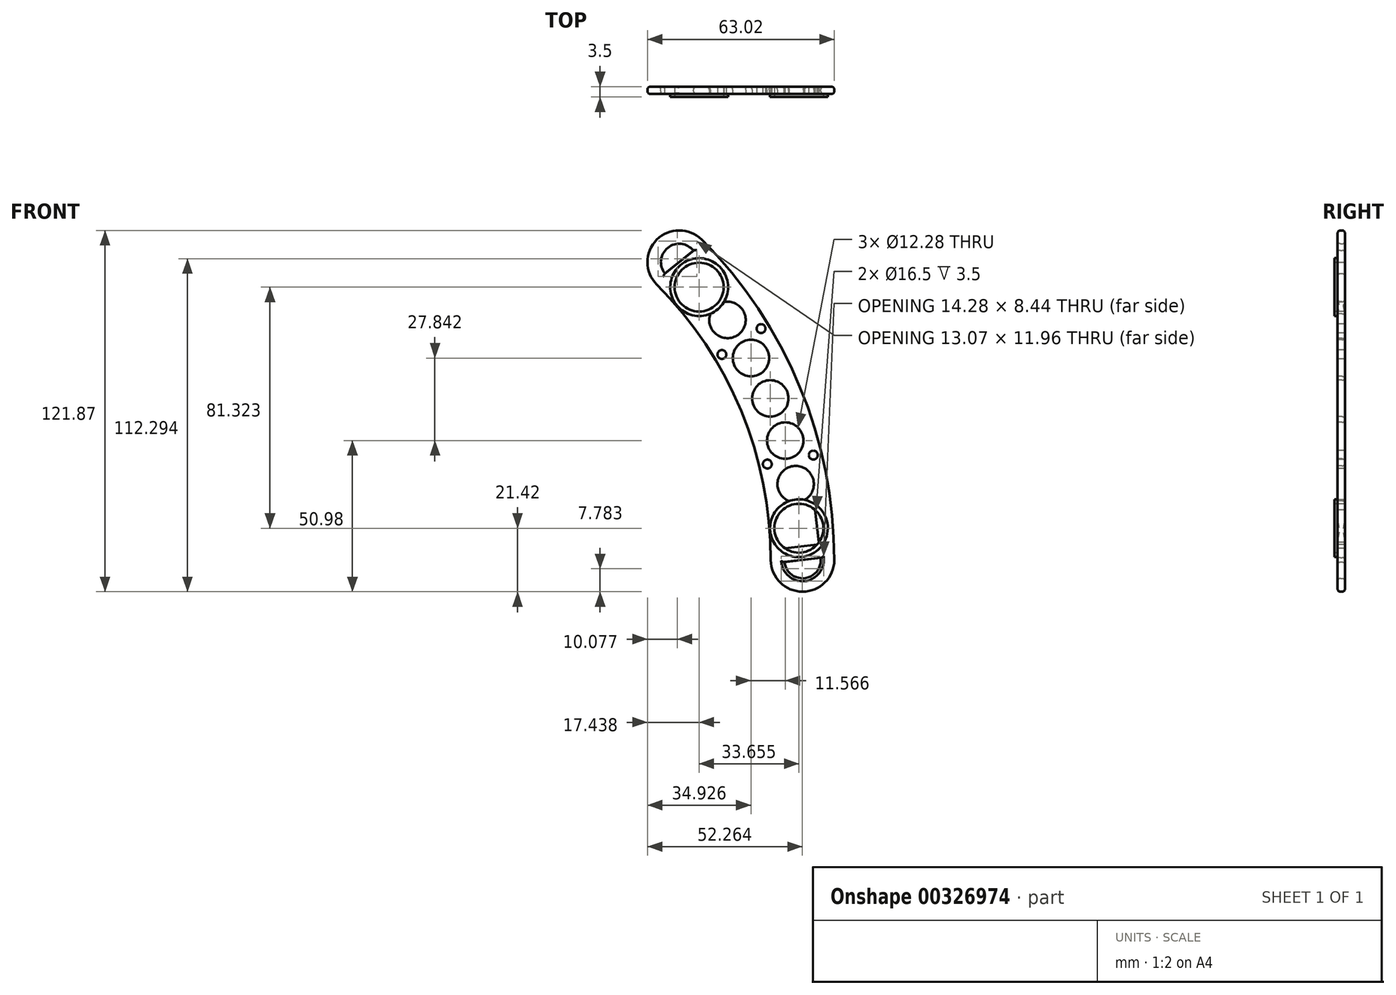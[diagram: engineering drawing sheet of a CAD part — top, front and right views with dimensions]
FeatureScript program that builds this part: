
annotation { "Feature Type Name" : "Feature", "Feature Type Description" : "" }
export const myFeature = defineFeature(function(context is Context, id is Id, definition is map)
    precondition{}
    {
        {
            var Q0;
            Q0=qCreatedBy(makeId("Front.planeOp"),FACE);
            var sketch = newSketch(context, id + "F0", { "sketchPlane" : qUnion([Q0])});
            skCircle(sketch, "E0", {"center": v(0, 0) * mm, "radius": 152.8 * mm});
            skCircle(sketch, "E1", {"center": v(0, 0) * mm, "radius": 131.4 * mm});
            skLineSegment(sketch, "E2", {"start": v(0, 0) * mm, "end": v(152.8, 0) * mm, "construction": true});
            skLineSegment(sketch, "E3", {"start": v(0, 0) * mm, "end": v(108.04, 108.04) * mm, "construction": true});
            skPoint(sketch, "E4", {"position": v(92.9, 92.9) * mm});
            skPoint(sketch, "E5", {"position": v(108.04, 108.04) * mm});
            skPoint(sketch, "E6", {"position": v(131.4, 0) * mm});
            skPoint(sketch, "E7", {"position": v(152.8, 0) * mm});
            skCircle(sketch, "E8", {"center": v(100.47, 100.47) * mm, "radius": 10.7 * mm});
            skCircle(sketch, "E9", {"center": v(142.1, 0) * mm, "radius": 10.7 * mm});
            skLineSegment(sketch, "E10", {"start": v(142.1, 0) * mm, "end": v(148.23, 0.7) * mm});
            skLineSegment(sketch, "E11", {"start": v(142.1, 0) * mm, "end": v(135.94, -0.7) * mm});
            skLineSegment(sketch, "E12", {"start": v(148.23, 0.7) * mm, "end": v(144.58, 32.71) * mm});
            skLineSegment(sketch, "E13", {"start": v(135.94, -0.7) * mm, "end": v(132.3, 31.31) * mm});
            skLineSegment(sketch, "E14", {"start": v(132.3, 31.31) * mm, "end": v(144.58, 32.71) * mm});
            skLineSegment(sketch, "E15", {"start": v(100.47, 100.47) * mm, "end": v(105.3, 104.33) * mm});
            skLineSegment(sketch, "E16", {"start": v(100.47, 100.47) * mm, "end": v(95.64, 96.62) * mm});
            skLineSegment(sketch, "E17", {"start": v(120.53, 75.25) * mm, "end": v(125.41, 79.16) * mm});
            skLineSegment(sketch, "E18", {"start": v(120.53, 75.25) * mm, "end": v(115.75, 71.44) * mm});
            skLineSegment(sketch, "E19", {"start": v(105.3, 104.33) * mm, "end": v(125.41, 79.16) * mm});
            skLineSegment(sketch, "E20", {"start": v(95.64, 96.62) * mm, "end": v(115.75, 71.44) * mm});
            skLineSegment(sketch, "E21", {"start": v(135.42, 3.88) * mm, "end": v(147.7, 5.28) * mm});
            skLineSegment(sketch, "E22", {"start": v(132.82, 26.73) * mm, "end": v(145.1, 28.13) * mm});
            skLineSegment(sketch, "E23", {"start": v(112.88, 75.04) * mm, "end": v(122.53, 82.76) * mm});
            skLineSegment(sketch, "E24", {"start": v(98.52, 93.01) * mm, "end": v(108.18, 100.73) * mm});
            skCircle(sketch, "E25", {"center": v(0, 0) * mm, "radius": 148.23 * mm, "construction": true});
            skCircle(sketch, "E26", {"center": v(0, 0) * mm, "radius": 135.95 * mm, "construction": true});
            skCircle(sketch, "E27", {"center": v(141.82, 2.29) * mm, "radius": 1 * mm});
            skCircle(sketch, "E28", {"center": v(138.7, 29.72) * mm, "radius": 1 * mm});
            skCircle(sketch, "E29", {"center": v(140.86, 10.72) * mm, "radius": 6.18 * mm});
            skLineSegment(sketch, "E30", {"start": v(122.53, 82.76) * mm, "end": v(115.75, 71.44) * mm, "construction": true});
            skLineSegment(sketch, "E31", {"start": v(112.88, 75.04) * mm, "end": v(125.41, 79.16) * mm, "construction": true});
            skCircle(sketch, "E32", {"center": v(101.91, 98.67) * mm, "radius": 1 * mm});
            skCircle(sketch, "E33", {"center": v(119.14, 77.1) * mm, "radius": 1 * mm});
            skCircle(sketch, "E34", {"center": v(107.2, 92.04) * mm, "radius": 6.18 * mm});
            skLineSegment(sketch, "E35", {"start": v(132.82, 26.73) * mm, "end": v(144.58, 32.71) * mm, "construction": true});
            skLineSegment(sketch, "E36", {"start": v(145.1, 28.13) * mm, "end": v(132.3, 31.31) * mm, "construction": true});
            skCircle(sketch, "E37", {"center": v(100.47, 100.47) * mm, "radius": 6.18 * mm});
            skCircle(sketch, "E38", {"center": v(142.1, 0) * mm, "radius": 6.19 * mm});
            skLineSegment(sketch, "E39", {"start": v(135.42, 3.88) * mm, "end": v(148.23, 0.7) * mm, "construction": true});
            skLineSegment(sketch, "E40", {"start": v(147.7, 5.28) * mm, "end": v(135.94, -0.7) * mm, "construction": true});
            skLineSegment(sketch, "E41", {"start": v(148.23, 0.7) * mm, "end": v(148.24, 0.7) * mm});
            skSolve(sketch);
        }
        {
            var Q0;
            {var subQ16=sQuery(id+"F0.wireOp",EDGE,"E18");Q0=makeQuery(id+"F0.imprint","IMPRINT",FACE,{"disambiguationData":[TD([[makeQuery(id+"F0.imprint","IMPRINT",EDGE,{"derivedFrom":subQ16}),1.0]])]});}
            var Q1;
            {var subQ14=sQuery(id+"F0.wireOp",EDGE,"E17");Q1=makeQuery(id+"F0.imprint","IMPRINT",FACE,{"disambiguationData":[TD([[makeQuery(id+"F0.imprint","IMPRINT",EDGE,{"derivedFrom":subQ14}),-1.0]])]});}
            var Q2;
            {var subQ3=sQuery(id+"F0.wireOp",EDGE,"oQQra7B9-EMDj-B2YQ-GpEd-beqhVWcHA2Qh");var subQ5=sQuery(id+"F0.wireOp",EDGE,"E22");var subQ9=makeQuery(id+"F0.imprint","INTERSECT",VERTEX,{"derivedFrom":[subQ3,subQ5]});Q2=makeQuery(id+"F0.imprint","IMPRINT",FACE,{"disambiguationData":[TD([[makeQuery(id+"F0.imprint","IMPRINT",EDGE,{"disambiguationData":[TD([[subQ9,-1.0]])],"derivedFrom":subQ3}),-1.0]])]});}
            var Q3;
            {var subQ3=sQuery(id+"F0.wireOp",EDGE,"oQQra7B9-EMDj-B2YQ-GpEd-beqhVWcHA2Qh");var subQ5=sQuery(id+"F0.wireOp",EDGE,"E22");var subQ9=makeQuery(id+"F0.imprint","INTERSECT",VERTEX,{"derivedFrom":[subQ3,subQ5]});Q3=makeQuery(id+"F0.imprint","IMPRINT",FACE,{"disambiguationData":[TD([[makeQuery(id+"F0.imprint","IMPRINT",EDGE,{"disambiguationData":[TD([[subQ9,-1.0]])],"derivedFrom":subQ3}),1.0]])]});}
            var Q4;
            {var subQ5=sQuery(id+"F0.wireOp",EDGE,"E9");var subQ8=makeQuery(id+"F0.imprint","INTERSECT",VERTEX,{"derivedFrom":[sQuery(id+"F0.wireOp",EDGE,"E1"),subQ5]});Q4=makeQuery(id+"F0.imprint","IMPRINT",FACE,{"disambiguationData":[TD([[makeQuery(id+"F0.imprint","IMPRINT",EDGE,{"disambiguationData":[TD([[subQ8,1.0]])],"derivedFrom":subQ5}),1.0]])]});}
            var Q5;
            {var subQ1=sQuery(id+"F0.wireOp",EDGE,"E9");var subQ5=makeQuery(id+"F0.imprint","INTERSECT",VERTEX,{"derivedFrom":[sQuery(id+"F0.wireOp",EDGE,"E0"),subQ1]});Q5=makeQuery(id+"F0.imprint","IMPRINT",FACE,{"disambiguationData":[TD([[makeQuery(id+"F0.imprint","IMPRINT",EDGE,{"disambiguationData":[TD([[subQ5,-1.0]])],"derivedFrom":subQ1}),1.0]])]});}
            var Q6;
            {var subQ1=sQuery(id+"F0.wireOp",EDGE,"E13");var subQ3=sQuery(id+"F0.wireOp",EDGE,"E21");var subQ4=makeQuery(id+"F0.imprint","INTERSECT",VERTEX,{"derivedFrom":[subQ1,subQ3]});Q6=makeQuery(id+"F0.imprint","IMPRINT",FACE,{"disambiguationData":[TD([[makeQuery(id+"F0.imprint","IMPRINT",EDGE,{"disambiguationData":[TD([[subQ4,-1.0]])],"derivedFrom":subQ3}),-1.0]])]});}
            var Q7;
            {var subQ1=sQuery(id+"F0.wireOp",EDGE,"E12");var subQ3=sQuery(id+"F0.wireOp",EDGE,"E21");var subQ4=makeQuery(id+"F0.imprint","INTERSECT",VERTEX,{"derivedFrom":[subQ1,subQ3]});Q7=makeQuery(id+"F0.imprint","IMPRINT",FACE,{"disambiguationData":[TD([[makeQuery(id+"F0.imprint","IMPRINT",EDGE,{"disambiguationData":[TD([[subQ4,1.0]])],"derivedFrom":subQ3}),-1.0]])]});}
            var Q8;
            {var subQ4=sQuery(id+"F0.wireOp",EDGE,"E8");var subQ5=makeQuery(id+"F0.imprint","INTERSECT",VERTEX,{"derivedFrom":[sQuery(id+"F0.wireOp",EDGE,"E0"),subQ4]});Q8=makeQuery(id+"F0.imprint","IMPRINT",FACE,{"disambiguationData":[TD([[makeQuery(id+"F0.imprint","IMPRINT",EDGE,{"disambiguationData":[TD([[subQ5,-1.0]])],"derivedFrom":subQ4}),1.0]])]});}
            var Q9;
            {var subQ5=sQuery(id+"F0.wireOp",EDGE,"E8");var subQ9=makeQuery(id+"F0.imprint","INTERSECT",VERTEX,{"derivedFrom":[sQuery(id+"F0.wireOp",EDGE,"E1"),subQ5]});Q9=makeQuery(id+"F0.imprint","IMPRINT",FACE,{"disambiguationData":[TD([[makeQuery(id+"F0.imprint","IMPRINT",EDGE,{"disambiguationData":[TD([[subQ9,1.0]])],"derivedFrom":subQ5}),1.0]])]});}
            var Q10;
            {var subQ1=sQuery(id+"F0.wireOp",EDGE,"E20");var subQ3=sQuery(id+"F0.wireOp",EDGE,"E24");var subQ4=makeQuery(id+"F0.imprint","INTERSECT",VERTEX,{"derivedFrom":[subQ1,subQ3]});Q10=makeQuery(id+"F0.imprint","IMPRINT",FACE,{"disambiguationData":[TD([[makeQuery(id+"F0.imprint","IMPRINT",EDGE,{"disambiguationData":[TD([[subQ4,-1.0]])],"derivedFrom":subQ3}),1.0]])]});}
            var Q11;
            {var subQ4=sQuery(id+"F0.wireOp",EDGE,"E16");Q11=makeQuery(id+"F0.imprint","IMPRINT",FACE,{"disambiguationData":[TD([[makeQuery(id+"F0.imprint","IMPRINT",EDGE,{"derivedFrom":subQ4}),1.0]])]});}
            var Q12;
            {var subQ0=sQuery(id+"F0.wireOp",EDGE,"E15");Q12=makeQuery(id+"F0.imprint","IMPRINT",FACE,{"disambiguationData":[TD([[makeQuery(id+"F0.imprint","IMPRINT",EDGE,{"derivedFrom":subQ0}),-1.0]])]});}
            var Q13;
            {var subQ1=sQuery(id+"F0.wireOp",EDGE,"E19");var subQ3=sQuery(id+"F0.wireOp",EDGE,"E24");var subQ4=makeQuery(id+"F0.imprint","INTERSECT",VERTEX,{"derivedFrom":[subQ1,subQ3]});Q13=makeQuery(id+"F0.imprint","IMPRINT",FACE,{"disambiguationData":[TD([[makeQuery(id+"F0.imprint","IMPRINT",EDGE,{"disambiguationData":[TD([[subQ4,1.0]])],"derivedFrom":subQ3}),1.0]])]});}
            var Q14;
            {var subQ1=sQuery(id+"F0.wireOp",EDGE,"E18");Q14=makeQuery(id+"F0.imprint","IMPRINT",FACE,{"disambiguationData":[TD([[makeQuery(id+"F0.imprint","IMPRINT",EDGE,{"derivedFrom":subQ1}),-1.0]])]});}
            var Q15;
            {var subQ1=sQuery(id+"F0.wireOp",EDGE,"E17");Q15=makeQuery(id+"F0.imprint","IMPRINT",FACE,{"disambiguationData":[TD([[makeQuery(id+"F0.imprint","IMPRINT",EDGE,{"derivedFrom":subQ1}),1.0]])]});}
            var Q16;
            {var subQ0=sQuery(id+"F0.wireOp",EDGE,"E14");Q16=makeQuery(id+"F0.imprint","IMPRINT",FACE,{"disambiguationData":[TD([[makeQuery(id+"F0.imprint","IMPRINT",EDGE,{"derivedFrom":subQ0}),-1.0]])]});}
            var Q17;
            {var subQ5=sQuery(id+"F0.wireOp",EDGE,"E10");Q17=makeQuery(id+"F0.imprint","IMPRINT",FACE,{"disambiguationData":[TD([[makeQuery(id+"F0.imprint","IMPRINT",EDGE,{"derivedFrom":subQ5}),1.0]])]});}
            var Q18;
            Q18=makeQuery(id+"F0.imprint","IMPRINT",FACE,{"disambiguationData":[TD([[makeQuery(id+"F0.imprint","IMPRINT",EDGE,{"derivedFrom":sQuery(id+"F0.wireOp",EDGE,"E27")}),-1.0]])]});
            var Q19;
            {var subQ0=sQuery(id+"F0.wireOp",EDGE,"E41");Q19=makeQuery(id+"F0.imprint","IMPRINT",FACE,{"disambiguationData":[TD([[makeQuery(id+"F0.imprint","IMPRINT",EDGE,{"derivedFrom":subQ0}),1.0]])]});}
            extrude(context, id + "F1", {"entities" : qUnion([Q0, Q1, Q2, Q3, Q4, Q5, Q6, Q7, Q8, Q9, Q10, Q11, Q12, Q13, Q14, Q15, Q16, Q17, Q18, Q19]), "depth" : 2.5 * mm});
        }
        {
            var Q0;
            Q0=makeQuery(id+"F1.opExtrude","CAP_FACE",FACE,{"disambiguationData":[OSD([sQuery(id+"F0.wireOp",EDGE,"E0"),sQuery(id+"F0.wireOp",EDGE,"E1"),sQuery(id+"F0.wireOp",EDGE,"E8"),sQuery(id+"F0.wireOp",EDGE,"E9"),sQuery(id+"F0.wireOp",EDGE,"E10"),sQuery(id+"F0.wireOp",EDGE,"E11"),sQuery(id+"F0.wireOp",EDGE,"E12"),sQuery(id+"F0.wireOp",EDGE,"E13"),sQuery(id+"F0.wireOp",EDGE,"E15"),sQuery(id+"F0.wireOp",EDGE,"E16"),sQuery(id+"F0.wireOp",EDGE,"E19"),sQuery(id+"F0.wireOp",EDGE,"E20"),sQuery(id+"F0.wireOp",EDGE,"E21"),sQuery(id+"F0.wireOp",EDGE,"E22"),sQuery(id+"F0.wireOp",EDGE,"E23"),sQuery(id+"F0.wireOp",EDGE,"E24"),sQuery(id+"F0.wireOp",EDGE,"E27"),sQuery(id+"F0.wireOp",EDGE,"E28"),sQuery(id+"F0.wireOp",EDGE,"E32"),sQuery(id+"F0.wireOp",EDGE,"E33"),sQuery(id+"F0.wireOp",EDGE,"E37"),sQuery(id+"F0.wireOp",EDGE,"E38")])],"isStart":false});
            var sketch = newSketch(context, id + "F2", { "sketchPlane" : qUnion([Q0])});
            skCircle(sketch, "E42", {"center": v(136.26, 40.28) * mm, "radius": 6.14 * mm});
            skCircle(sketch, "E43", {"center": v(124.7, 68.12) * mm, "radius": 6.14 * mm});
            skCircle(sketch, "E44", {"center": v(131.22, 54.5) * mm, "radius": 6.14 * mm});
            skCircle(sketch, "E45", {"center": v(0, 0) * mm, "radius": 142.1 * mm, "construction": true});
            skLineSegment(sketch, "E46", {"start": v(0, 0) * mm, "end": v(136.26, 40.28) * mm, "construction": true});
            skLineSegment(sketch, "E47", {"start": v(0, 0) * mm, "end": v(131.22, 54.5) * mm, "construction": true});
            skLineSegment(sketch, "E48", {"start": v(0, 0) * mm, "end": v(124.7, 68.12) * mm, "construction": true});
            skCircle(sketch, "E49", {"center": v(0, 0) * mm, "radius": 152.8 * mm, "construction": true});
            skCircle(sketch, "E50", {"center": v(0, 0) * mm, "radius": 131.4 * mm, "construction": true});
            skCircle(sketch, "E51", {"center": v(0, 0) * mm, "radius": 135.95 * mm, "construction": true});
            skCircle(sketch, "E52", {"center": v(0, 0) * mm, "radius": 148.23 * mm, "construction": true});
            skLineSegment(sketch, "E53", {"start": v(112.88, 75.04) * mm, "end": v(119.3, 65.18) * mm, "construction": true});
            skLineSegment(sketch, "E54", {"start": v(119.3, 65.18) * mm, "end": v(118, 79.14) * mm, "construction": true});
            skLineSegment(sketch, "E55", {"start": v(118, 79.14) * mm, "end": v(130.08, 71.07) * mm, "construction": true});
            skLineSegment(sketch, "E56", {"start": v(130.08, 71.07) * mm, "end": v(122.53, 82.76) * mm, "construction": true});
            skLineSegment(sketch, "E57", {"start": v(122.53, 82.76) * mm, "end": v(118, 79.14) * mm});
            skLineSegment(sketch, "E58", {"start": v(112.88, 75.04) * mm, "end": v(118, 79.14) * mm});
            skLineSegment(sketch, "E59", {"start": v(126.3, 76.91) * mm, "end": v(130.43, 79.57) * mm, "construction": true});
            skCircle(sketch, "E60", {"center": v(128.1, 78.07) * mm, "radius": 1 * mm});
            skLineSegment(sketch, "E61", {"start": v(130.37, 38.54) * mm, "end": v(132.82, 26.73) * mm});
            skLineSegment(sketch, "E62", {"start": v(145.1, 28.13) * mm, "end": v(142.22, 41.78) * mm});
            skLineSegment(sketch, "E63", {"start": v(131.6, 32.64) * mm, "end": v(127.49, 31.79) * mm});
            skLineSegment(sketch, "E64", {"start": v(143.66, 34.96) * mm, "end": v(148.5, 35.98) * mm});
            skCircle(sketch, "E65", {"center": v(130.21, 32.35) * mm, "radius": 1 * mm});
            skCircle(sketch, "E66", {"center": v(145.71, 35.4) * mm, "radius": 1 * mm});
            skLineSegment(sketch, "E67", {"start": v(116.1, 70.11) * mm, "end": v(112.55, 67.8) * mm, "construction": true});
            skCircle(sketch, "E68", {"center": v(114.87, 69.32) * mm, "radius": 1 * mm});
            skLineSegment(sketch, "E69", {"start": v(0, 0) * mm, "end": v(116.76, 80.97) * mm, "construction": true});
            skLineSegment(sketch, "E70", {"start": v(0, 0) * mm, "end": v(139.77, 25.6) * mm, "construction": true});
            skCircle(sketch, "E71", {"center": v(139.77, 25.6) * mm, "radius": 6.14 * mm});
            skCircle(sketch, "E72", {"center": v(116.76, 80.97) * mm, "radius": 6.14 * mm});
            skSolve(sketch);
        }
        {
            var Q0;
            Q0=makeQuery(id+"F2.imprint","IMPRINT",FACE,{"disambiguationData":[TD([[makeQuery(id+"F2.imprint","IMPRINT",EDGE,{"derivedFrom":sQuery(id+"F2.wireOp",EDGE,"E43")}),1.0]])]});
            var Q1;
            Q1=makeQuery(id+"F2.imprint","IMPRINT",FACE,{"disambiguationData":[TD([[makeQuery(id+"F2.imprint","IMPRINT",EDGE,{"derivedFrom":sQuery(id+"F2.wireOp",EDGE,"E44")}),1.0]])]});
            var Q2;
            Q2=makeQuery(id+"F2.imprint","IMPRINT",FACE,{"disambiguationData":[TD([[makeQuery(id+"F2.imprint","IMPRINT",EDGE,{"derivedFrom":sQuery(id+"F2.wireOp",EDGE,"E42")}),1.0]])]});
            var Q3;
            {var subQ0=sQuery(id+"F2.wireOp",EDGE,"E56");var subQ1=sQuery(id+"F2.wireOp",EDGE,"E43");var subQ2=makeQuery(id+"F2.imprint","INTERSECT",VERTEX,{"derivedFrom":[subQ1,subQ0]});Q3=makeQuery(id+"F2.imprint","IMPRINT",FACE,{"disambiguationData":[TD([[makeQuery(id+"F2.imprint","IMPRINT",EDGE,{"disambiguationData":[TD([[subQ2,-1.0]])],"derivedFrom":subQ1}),1.0]])]});}
            var Q4;
            {var subQ0=sQuery(id+"F2.wireOp",EDGE,"E54");var subQ1=sQuery(id+"F2.wireOp",EDGE,"E43");var subQ3=makeQuery(id+"F2.imprint","INTERSECT",VERTEX,{"derivedFrom":[subQ1,subQ0]});Q4=makeQuery(id+"F2.imprint","IMPRINT",FACE,{"disambiguationData":[TD([[makeQuery(id+"F2.imprint","IMPRINT",EDGE,{"disambiguationData":[TD([[subQ3,-1.0]])],"derivedFrom":subQ1}),1.0]])]});}
            var Q5;
            Q5=makeQuery(id+"F2.imprint","IMPRINT",FACE,{"disambiguationData":[TD([[makeQuery(id+"F2.imprint","IMPRINT",EDGE,{"derivedFrom":sQuery(id+"F2.wireOp",EDGE,"6Q9i7ZKX-M5Zn-dDvE-S5ua-DKoOSJd4rO0q")}),1.0]])]});
            var Q6;
            Q6=makeQuery(id+"F2.imprint","IMPRINT",FACE,{"disambiguationData":[TD([[makeQuery(id+"F2.imprint","IMPRINT",EDGE,{"derivedFrom":sQuery(id+"F2.wireOp",EDGE,"E60")}),1.0]])]});
            var Q7;
            Q7=makeQuery(id+"F2.imprint","IMPRINT",FACE,{"disambiguationData":[TD([[makeQuery(id+"F2.imprint","IMPRINT",EDGE,{"derivedFrom":sQuery(id+"F2.wireOp",EDGE,"E68")}),1.0]])]});
            var Q8;
            {var subQ0=sQuery(id+"F2.wireOp",EDGE,"E66");var subQ1=sQuery(id+"F2.wireOp",EDGE,"E64");var subQ2=makeQuery(id+"F2.imprint","INTERSECT",VERTEX,{"disambiguationData":[OD(0.0)],"derivedFrom":[subQ1,subQ0]});Q8=makeQuery(id+"F2.imprint","IMPRINT",FACE,{"disambiguationData":[TD([[makeQuery(id+"F2.imprint","IMPRINT",EDGE,{"disambiguationData":[TD([[subQ2,-1.0]])],"derivedFrom":subQ1}),1.0]])]});}
            var Q9;
            {var subQ0=sQuery(id+"F2.wireOp",EDGE,"E66");var subQ1=sQuery(id+"F2.wireOp",EDGE,"E64");var subQ2=makeQuery(id+"F2.imprint","INTERSECT",VERTEX,{"disambiguationData":[OD(0.0)],"derivedFrom":[subQ1,subQ0]});Q9=makeQuery(id+"F2.imprint","IMPRINT",FACE,{"disambiguationData":[TD([[makeQuery(id+"F2.imprint","IMPRINT",EDGE,{"disambiguationData":[TD([[subQ2,-1.0]])],"derivedFrom":subQ1}),-1.0]])]});}
            var Q10;
            {var subQ0=sQuery(id+"F2.wireOp",EDGE,"E65");var subQ1=sQuery(id+"F2.wireOp",EDGE,"E63");var subQ2=makeQuery(id+"F2.imprint","INTERSECT",VERTEX,{"disambiguationData":[OD(0.0)],"derivedFrom":[subQ1,subQ0]});Q10=makeQuery(id+"F2.imprint","IMPRINT",FACE,{"disambiguationData":[TD([[makeQuery(id+"F2.imprint","IMPRINT",EDGE,{"disambiguationData":[TD([[subQ2,-1.0]])],"derivedFrom":subQ1}),1.0]])]});}
            var Q11;
            {var subQ0=sQuery(id+"F2.wireOp",EDGE,"E65");var subQ1=sQuery(id+"F2.wireOp",EDGE,"E63");var subQ2=makeQuery(id+"F2.imprint","INTERSECT",VERTEX,{"disambiguationData":[OD(0.0)],"derivedFrom":[subQ1,subQ0]});Q11=makeQuery(id+"F2.imprint","IMPRINT",FACE,{"disambiguationData":[TD([[makeQuery(id+"F2.imprint","IMPRINT",EDGE,{"disambiguationData":[TD([[subQ2,-1.0]])],"derivedFrom":subQ1}),-1.0]])]});}
            extrude(context, id + "F3", {"entities" : qUnion([Q0, Q1, Q2, Q3, Q4, Q5, Q6, Q7, Q8, Q9, Q10, Q11]), "operationType" : NewBodyOperationType.REMOVE, "oppositeDirection" : true, "depth" : 25 * mm});
        }
        {
            var Q0;
            Q0=makeQuery(id+"F1.opExtrude","CAP_EDGE",EDGE,{"disambiguationData":[OSD([sQuery(id+"F0.wireOp",EDGE,"E38")])],"isStart":true});
            var Q1;
            Q1=makeQuery(id+"F1.opExtrude","CAP_EDGE",EDGE,{"disambiguationData":[OSD([sQuery(id+"F0.wireOp",EDGE,"E38")])],"isStart":false});
            var Q2;
            Q2=makeQuery(id+"F1.opExtrude","CAP_EDGE",EDGE,{"disambiguationData":[OSD([sQuery(id+"F0.wireOp",EDGE,"E9")])],"isStart":true});
            var Q3;
            Q3=makeQuery(id+"F1.opExtrude","CAP_EDGE",EDGE,{"disambiguationData":[OSD([sQuery(id+"F0.wireOp",EDGE,"E0")])],"isStart":false});
            var Q4;
            Q4=makeQuery(id+"F1.opExtrude","CAP_EDGE",EDGE,{"disambiguationData":[OSD([sQuery(id+"F0.wireOp",EDGE,"E37")])],"isStart":false});
            var Q5;
            Q5=makeQuery(id+"F1.opExtrude","CAP_EDGE",EDGE,{"disambiguationData":[OSD([sQuery(id+"F0.wireOp",EDGE,"E37")])],"isStart":true});
            var Q6;
            Q6=makeQuery(id+"F3.boolean.opBoolean","COPY",EDGE,{"derivedFrom":makeQuery(id+"F3.opExtrude","CAP_EDGE",EDGE,{"disambiguationData":[OSD([sQuery(id+"F2.wireOp",EDGE,"E43")])],"isStart":true})});
            var Q7;
            Q7=makeQuery(id+"F3.boolean.opBoolean","COPY",EDGE,{"derivedFrom":makeQuery(id+"F3.opExtrude","CAP_EDGE",EDGE,{"disambiguationData":[OSD([sQuery(id+"F2.wireOp",EDGE,"E44")])],"isStart":true})});
            var Q8;
            Q8=makeQuery(id+"F3.boolean.opBoolean","COPY",EDGE,{"derivedFrom":makeQuery(id+"F3.opExtrude","CAP_EDGE",EDGE,{"disambiguationData":[OSD([sQuery(id+"F2.wireOp",EDGE,"E42")])],"isStart":true})});
            var Q9;
            Q9=makeQuery(id+"F3.boolean.opBoolean","INTERSECT",EDGE,{"derivedFrom":[makeQuery(id+"F1.opExtrude","CAP_FACE",FACE,{"disambiguationData":[OSD([sQuery(id+"F0.wireOp",EDGE,"E0"),sQuery(id+"F0.wireOp",EDGE,"E1"),sQuery(id+"F0.wireOp",EDGE,"E8"),sQuery(id+"F0.wireOp",EDGE,"E9"),sQuery(id+"F0.wireOp",EDGE,"E10"),sQuery(id+"F0.wireOp",EDGE,"E11"),sQuery(id+"F0.wireOp",EDGE,"E12"),sQuery(id+"F0.wireOp",EDGE,"E13"),sQuery(id+"F0.wireOp",EDGE,"E15"),sQuery(id+"F0.wireOp",EDGE,"E16"),sQuery(id+"F0.wireOp",EDGE,"E19"),sQuery(id+"F0.wireOp",EDGE,"E20"),sQuery(id+"F0.wireOp",EDGE,"E21"),sQuery(id+"F0.wireOp",EDGE,"E22"),sQuery(id+"F0.wireOp",EDGE,"E23"),sQuery(id+"F0.wireOp",EDGE,"E24"),sQuery(id+"F0.wireOp",EDGE,"E27"),sQuery(id+"F0.wireOp",EDGE,"E28"),sQuery(id+"F0.wireOp",EDGE,"E32"),sQuery(id+"F0.wireOp",EDGE,"E33"),sQuery(id+"F0.wireOp",EDGE,"E37"),sQuery(id+"F0.wireOp",EDGE,"E38")])],"isStart":true}),makeQuery(id+"F3.opExtrude","SWEPT_FACE",FACE,{"disambiguationData":[OSD([sQuery(id+"F2.wireOp",EDGE,"E43")])]})]});
            var Q10;
            Q10=makeQuery(id+"F3.boolean.opBoolean","INTERSECT",EDGE,{"derivedFrom":[makeQuery(id+"F1.opExtrude","CAP_FACE",FACE,{"disambiguationData":[OSD([sQuery(id+"F0.wireOp",EDGE,"E0"),sQuery(id+"F0.wireOp",EDGE,"E1"),sQuery(id+"F0.wireOp",EDGE,"E8"),sQuery(id+"F0.wireOp",EDGE,"E9"),sQuery(id+"F0.wireOp",EDGE,"E10"),sQuery(id+"F0.wireOp",EDGE,"E11"),sQuery(id+"F0.wireOp",EDGE,"E12"),sQuery(id+"F0.wireOp",EDGE,"E13"),sQuery(id+"F0.wireOp",EDGE,"E15"),sQuery(id+"F0.wireOp",EDGE,"E16"),sQuery(id+"F0.wireOp",EDGE,"E19"),sQuery(id+"F0.wireOp",EDGE,"E20"),sQuery(id+"F0.wireOp",EDGE,"E21"),sQuery(id+"F0.wireOp",EDGE,"E22"),sQuery(id+"F0.wireOp",EDGE,"E23"),sQuery(id+"F0.wireOp",EDGE,"E24"),sQuery(id+"F0.wireOp",EDGE,"E27"),sQuery(id+"F0.wireOp",EDGE,"E28"),sQuery(id+"F0.wireOp",EDGE,"E32"),sQuery(id+"F0.wireOp",EDGE,"E33"),sQuery(id+"F0.wireOp",EDGE,"E37"),sQuery(id+"F0.wireOp",EDGE,"E38")])],"isStart":true}),makeQuery(id+"F3.opExtrude","SWEPT_FACE",FACE,{"disambiguationData":[OSD([sQuery(id+"F2.wireOp",EDGE,"E44")])]})]});
            var Q11;
            Q11=makeQuery(id+"F3.boolean.opBoolean","INTERSECT",EDGE,{"derivedFrom":[makeQuery(id+"F1.opExtrude","CAP_FACE",FACE,{"disambiguationData":[OSD([sQuery(id+"F0.wireOp",EDGE,"E0"),sQuery(id+"F0.wireOp",EDGE,"E1"),sQuery(id+"F0.wireOp",EDGE,"E8"),sQuery(id+"F0.wireOp",EDGE,"E9"),sQuery(id+"F0.wireOp",EDGE,"E10"),sQuery(id+"F0.wireOp",EDGE,"E11"),sQuery(id+"F0.wireOp",EDGE,"E12"),sQuery(id+"F0.wireOp",EDGE,"E13"),sQuery(id+"F0.wireOp",EDGE,"E15"),sQuery(id+"F0.wireOp",EDGE,"E16"),sQuery(id+"F0.wireOp",EDGE,"E19"),sQuery(id+"F0.wireOp",EDGE,"E20"),sQuery(id+"F0.wireOp",EDGE,"E21"),sQuery(id+"F0.wireOp",EDGE,"E22"),sQuery(id+"F0.wireOp",EDGE,"E23"),sQuery(id+"F0.wireOp",EDGE,"E24"),sQuery(id+"F0.wireOp",EDGE,"E27"),sQuery(id+"F0.wireOp",EDGE,"E28"),sQuery(id+"F0.wireOp",EDGE,"E32"),sQuery(id+"F0.wireOp",EDGE,"E33"),sQuery(id+"F0.wireOp",EDGE,"E37"),sQuery(id+"F0.wireOp",EDGE,"E38")])],"isStart":true}),makeQuery(id+"F3.opExtrude","SWEPT_FACE",FACE,{"disambiguationData":[OSD([sQuery(id+"F2.wireOp",EDGE,"E42")])]})]});
            fillet(context, id + "F4", {"entities" : qUnion([Q0, Q1, Q2, Q3, Q4, Q5, Q6, Q7, Q8, Q9, Q10, Q11]), "radius" : 1 * mm, "tangentPropagation" : true, "allowEdgeOverflow" : false});
        }
        {
            var Q0;
            Q0=makeQuery(id+"F1.opExtrude","CAP_EDGE",EDGE,{"disambiguationData":[OSD([sQuery(id+"F0.wireOp",EDGE,"E15"),sQuery(id+"F0.wireOp",EDGE,"E16")])],"isStart":false});
            var Q1;
            Q1=makeQuery(id+"F1.opExtrude","CAP_EDGE",EDGE,{"disambiguationData":[OSD([sQuery(id+"F0.wireOp",EDGE,"E15"),sQuery(id+"F0.wireOp",EDGE,"E16")])],"isStart":true});
            var Q2;
            Q2=makeQuery(id+"F1.opExtrude","CAP_EDGE",EDGE,{"disambiguationData":[OSD([sQuery(id+"F0.wireOp",EDGE,"E10"),sQuery(id+"F0.wireOp",EDGE,"E11")])],"isStart":true});
            var Q3;
            Q3=makeQuery(id+"F1.opExtrude","CAP_EDGE",EDGE,{"disambiguationData":[OSD([sQuery(id+"F0.wireOp",EDGE,"E10"),sQuery(id+"F0.wireOp",EDGE,"E11")])],"isStart":false});
            fillet(context, id + "F5", {"entities" : qUnion([Q0, Q1, Q2, Q3]), "radius" : 0.5 * mm, "tangentPropagation" : true, "allowEdgeOverflow" : false});
        }
        {
            var Q0;
            {var subQ1=sQuery(id+"F0.wireOp",EDGE,"E9");var subQ6=sQuery(id+"F0.wireOp",EDGE,"E12");var subQ8=makeQuery(id+"F0.imprint","INTERSECT",VERTEX,{"derivedFrom":[subQ1,subQ6]});Q0=makeQuery(id+"F0.imprint","IMPRINT",FACE,{"disambiguationData":[TD([[makeQuery(id+"F0.imprint","IMPRINT",EDGE,{"disambiguationData":[TD([[subQ8,-1.0]])],"derivedFrom":subQ1}),1.0]])]});}
            var Q1;
            {var subQ0=sQuery(id+"F0.wireOp",EDGE,"E29");var subQ1=sQuery(id+"F0.wireOp",EDGE,"E9");var subQ2=makeQuery(id+"F0.imprint","INTERSECT",VERTEX,{"disambiguationData":[OD(0.0)],"derivedFrom":[subQ1,subQ0]});Q1=makeQuery(id+"F0.imprint","IMPRINT",FACE,{"disambiguationData":[TD([[makeQuery(id+"F0.imprint","IMPRINT",EDGE,{"disambiguationData":[TD([[subQ2,-1.0]])],"derivedFrom":subQ1}),-1.0]])]});}
            var Q2;
            {var subQ0=sQuery(id+"F0.wireOp",EDGE,"E29");var subQ1=sQuery(id+"F0.wireOp",EDGE,"E9");var subQ2=makeQuery(id+"F0.imprint","INTERSECT",VERTEX,{"disambiguationData":[OD(0.0)],"derivedFrom":[subQ1,subQ0]});Q2=makeQuery(id+"F0.imprint","IMPRINT",FACE,{"disambiguationData":[TD([[makeQuery(id+"F0.imprint","IMPRINT",EDGE,{"disambiguationData":[TD([[subQ2,-1.0]])],"derivedFrom":subQ1}),1.0]])]});}
            var Q3;
            {var subQ0=sQuery(id+"F0.wireOp",EDGE,"E29");var subQ1=makeQuery(id+"F0.imprint","INTERSECT",VERTEX,{"derivedFrom":[sQuery(id+"F0.wireOp",EDGE,"E21"),subQ0]});Q3=makeQuery(id+"F0.imprint","IMPRINT",FACE,{"disambiguationData":[TD([[makeQuery(id+"F0.imprint","IMPRINT",EDGE,{"disambiguationData":[TD([[subQ1,1.0]])],"derivedFrom":subQ0}),1.0]])]});}
            var Q4;
            {var subQ0=sQuery(id+"F0.wireOp",EDGE,"E29");var subQ1=sQuery(id+"F0.wireOp",EDGE,"E9");var subQ2=makeQuery(id+"F0.imprint","INTERSECT",VERTEX,{"disambiguationData":[OD(1.0)],"derivedFrom":[subQ1,subQ0]});Q4=makeQuery(id+"F0.imprint","IMPRINT",FACE,{"disambiguationData":[TD([[makeQuery(id+"F0.imprint","IMPRINT",EDGE,{"disambiguationData":[TD([[subQ2,-1.0]])],"derivedFrom":subQ1}),1.0]])]});}
            var Q5;
            {var subQ0=sQuery(id+"F0.wireOp",EDGE,"E38");var subQ1=sQuery(id+"F0.wireOp",EDGE,"E21");var subQ2=makeQuery(id+"F0.imprint","INTERSECT",VERTEX,{"disambiguationData":[OD(0.0)],"derivedFrom":[subQ1,subQ0]});Q5=makeQuery(id+"F0.imprint","IMPRINT",FACE,{"disambiguationData":[TD([[makeQuery(id+"F0.imprint","IMPRINT",EDGE,{"disambiguationData":[TD([[subQ2,-1.0]])],"derivedFrom":subQ1}),1.0]])]});}
            var Q6;
            {var subQ0=sQuery(id+"F0.wireOp",EDGE,"E29");var subQ1=sQuery(id+"F0.wireOp",EDGE,"E21");var subQ2=makeQuery(id+"F0.imprint","INTERSECT",VERTEX,{"derivedFrom":[subQ1,subQ0]});Q6=makeQuery(id+"F0.imprint","IMPRINT",FACE,{"disambiguationData":[TD([[makeQuery(id+"F0.imprint","IMPRINT",EDGE,{"disambiguationData":[TD([[subQ2,-1.0]])],"derivedFrom":subQ1}),1.0]])]});}
            var Q7;
            {var subQ0=sQuery(id+"F0.wireOp",EDGE,"E22");Q7=makeQuery(id+"F0.imprint","IMPRINT",FACE,{"disambiguationData":[TD([[makeQuery(id+"F0.imprint","IMPRINT",EDGE,{"derivedFrom":subQ0}),-1.0]])]});}
            var Q8;
            {var subQ0=sQuery(id+"F0.wireOp",EDGE,"E12");var subQ1=sQuery(id+"F0.wireOp",EDGE,"E9");var subQ2=makeQuery(id+"F0.imprint","INTERSECT",VERTEX,{"derivedFrom":[subQ1,subQ0]});Q8=makeQuery(id+"F0.imprint","IMPRINT",FACE,{"disambiguationData":[TD([[makeQuery(id+"F0.imprint","IMPRINT",EDGE,{"disambiguationData":[TD([[subQ2,-1.0]])],"derivedFrom":subQ1}),-1.0]])]});}
            var Q9;
            {var subQ0=sQuery(id+"F0.wireOp",EDGE,"E29");var subQ1=sQuery(id+"F0.wireOp",EDGE,"E9");var subQ2=makeQuery(id+"F0.imprint","INTERSECT",VERTEX,{"disambiguationData":[OD(1.0)],"derivedFrom":[subQ1,subQ0]});Q9=makeQuery(id+"F0.imprint","IMPRINT",FACE,{"disambiguationData":[TD([[makeQuery(id+"F0.imprint","IMPRINT",EDGE,{"disambiguationData":[TD([[subQ2,-1.0]])],"derivedFrom":subQ1}),-1.0]])]});}
            var Q10;
            {var subQ0=sQuery(id+"F0.wireOp",EDGE,"E23");Q10=makeQuery(id+"F0.imprint","IMPRINT",FACE,{"disambiguationData":[TD([[makeQuery(id+"F0.imprint","IMPRINT",EDGE,{"derivedFrom":subQ0}),1.0]])]});}
            var Q11;
            {var subQ0=sQuery(id+"F0.wireOp",EDGE,"E34");var subQ1=sQuery(id+"F0.wireOp",EDGE,"E8");var subQ2=makeQuery(id+"F0.imprint","INTERSECT",VERTEX,{"disambiguationData":[OD(0.0)],"derivedFrom":[subQ1,subQ0]});Q11=makeQuery(id+"F0.imprint","IMPRINT",FACE,{"disambiguationData":[TD([[makeQuery(id+"F0.imprint","IMPRINT",EDGE,{"disambiguationData":[TD([[subQ2,-1.0]])],"derivedFrom":subQ1}),-1.0]])]});}
            var Q12;
            {var subQ0=sQuery(id+"F0.wireOp",EDGE,"E34");var subQ1=sQuery(id+"F0.wireOp",EDGE,"E8");var subQ2=makeQuery(id+"F0.imprint","INTERSECT",VERTEX,{"disambiguationData":[OD(0.0)],"derivedFrom":[subQ1,subQ0]});Q12=makeQuery(id+"F0.imprint","IMPRINT",FACE,{"disambiguationData":[TD([[makeQuery(id+"F0.imprint","IMPRINT",EDGE,{"disambiguationData":[TD([[subQ2,-1.0]])],"derivedFrom":subQ1}),1.0]])]});}
            var Q13;
            {var subQ0=sQuery(id+"F0.wireOp",EDGE,"E34");var subQ1=sQuery(id+"F0.wireOp",EDGE,"E8");var subQ2=makeQuery(id+"F0.imprint","INTERSECT",VERTEX,{"disambiguationData":[OD(1.0)],"derivedFrom":[subQ1,subQ0]});Q13=makeQuery(id+"F0.imprint","IMPRINT",FACE,{"disambiguationData":[TD([[makeQuery(id+"F0.imprint","IMPRINT",EDGE,{"disambiguationData":[TD([[subQ2,-1.0]])],"derivedFrom":subQ1}),1.0]])]});}
            var Q14;
            {var subQ0=sQuery(id+"F0.wireOp",EDGE,"E34");var subQ1=sQuery(id+"F0.wireOp",EDGE,"E24");var subQ2=makeQuery(id+"F0.imprint","INTERSECT",VERTEX,{"derivedFrom":[subQ1,subQ0]});Q14=makeQuery(id+"F0.imprint","IMPRINT",FACE,{"disambiguationData":[TD([[makeQuery(id+"F0.imprint","IMPRINT",EDGE,{"disambiguationData":[TD([[subQ2,-1.0]])],"derivedFrom":subQ1}),-1.0]])]});}
            var Q15;
            {var subQ0=sQuery(id+"F0.wireOp",EDGE,"E34");var subQ1=makeQuery(id+"F0.imprint","INTERSECT",VERTEX,{"derivedFrom":[sQuery(id+"F0.wireOp",EDGE,"E24"),subQ0]});Q15=makeQuery(id+"F0.imprint","IMPRINT",FACE,{"disambiguationData":[TD([[makeQuery(id+"F0.imprint","IMPRINT",EDGE,{"disambiguationData":[TD([[subQ1,1.0]])],"derivedFrom":subQ0}),1.0]])]});}
            var Q16;
            {var subQ0=sQuery(id+"F0.wireOp",EDGE,"E37");var subQ1=sQuery(id+"F0.wireOp",EDGE,"E24");var subQ2=makeQuery(id+"F0.imprint","INTERSECT",VERTEX,{"disambiguationData":[OD(0.0)],"derivedFrom":[subQ1,subQ0]});Q16=makeQuery(id+"F0.imprint","IMPRINT",FACE,{"disambiguationData":[TD([[makeQuery(id+"F0.imprint","IMPRINT",EDGE,{"disambiguationData":[TD([[subQ2,-1.0]])],"derivedFrom":subQ1}),-1.0]])]});}
            var Q17;
            {var subQ1=sQuery(id+"F0.wireOp",EDGE,"E8");var subQ6=sQuery(id+"F0.wireOp",EDGE,"E20");var subQ9=makeQuery(id+"F0.imprint","INTERSECT",VERTEX,{"derivedFrom":[subQ1,subQ6]});Q17=makeQuery(id+"F0.imprint","IMPRINT",FACE,{"disambiguationData":[TD([[makeQuery(id+"F0.imprint","IMPRINT",EDGE,{"disambiguationData":[TD([[subQ9,-1.0]])],"derivedFrom":subQ1}),1.0]])]});}
            var Q18;
            {var subQ0=sQuery(id+"F0.wireOp",EDGE,"E34");var subQ1=sQuery(id+"F0.wireOp",EDGE,"E8");var subQ2=makeQuery(id+"F0.imprint","INTERSECT",VERTEX,{"disambiguationData":[OD(1.0)],"derivedFrom":[subQ1,subQ0]});Q18=makeQuery(id+"F0.imprint","IMPRINT",FACE,{"disambiguationData":[TD([[makeQuery(id+"F0.imprint","IMPRINT",EDGE,{"disambiguationData":[TD([[subQ2,-1.0]])],"derivedFrom":subQ1}),-1.0]])]});}
            var Q19;
            {var subQ0=sQuery(id+"F0.wireOp",EDGE,"E20");var subQ1=sQuery(id+"F0.wireOp",EDGE,"E8");var subQ2=makeQuery(id+"F0.imprint","INTERSECT",VERTEX,{"derivedFrom":[subQ1,subQ0]});Q19=makeQuery(id+"F0.imprint","IMPRINT",FACE,{"disambiguationData":[TD([[makeQuery(id+"F0.imprint","IMPRINT",EDGE,{"disambiguationData":[TD([[subQ2,-1.0]])],"derivedFrom":subQ1}),-1.0]])]});}
            extrude(context, id + "F6", {"entities" : qUnion([Q0, Q1, Q2, Q3, Q4, Q5, Q6, Q7, Q8, Q9, Q10, Q11, Q12, Q13, Q14, Q15, Q16, Q17, Q18, Q19]), "operationType" : NewBodyOperationType.ADD, "depth" : 2.5 * mm});
        }
        {
            var Q0;
            {var subQ0=sQuery(id+"F0.wireOp",EDGE,"E24");var subQ1=sQuery(id+"F0.wireOp",EDGE,"E23");var subQ2=sQuery(id+"F0.wireOp",EDGE,"E20");var subQ3=sQuery(id+"F0.wireOp",EDGE,"E19");var subQ4=sQuery(id+"F0.wireOp",EDGE,"E22");var subQ5=sQuery(id+"F0.wireOp",EDGE,"E21");var subQ6=sQuery(id+"F0.wireOp",EDGE,"E13");var subQ7=sQuery(id+"F0.wireOp",EDGE,"E12");Q0=makeQuery(id+"F6.boolean.opBoolean","MERGE",FACE,{"derivedFrom":[makeQuery(id+"F1.opExtrude","CAP_FACE",FACE,{"disambiguationData":[OSD([sQuery(id+"F0.wireOp",EDGE,"E0"),sQuery(id+"F0.wireOp",EDGE,"E1"),sQuery(id+"F0.wireOp",EDGE,"E8"),sQuery(id+"F0.wireOp",EDGE,"E9"),sQuery(id+"F0.wireOp",EDGE,"E10"),sQuery(id+"F0.wireOp",EDGE,"E11"),subQ7,subQ6,sQuery(id+"F0.wireOp",EDGE,"E15"),sQuery(id+"F0.wireOp",EDGE,"E16"),subQ3,subQ2,subQ5,subQ4,subQ1,subQ0,sQuery(id+"F0.wireOp",EDGE,"E27"),sQuery(id+"F0.wireOp",EDGE,"E28"),sQuery(id+"F0.wireOp",EDGE,"E32"),sQuery(id+"F0.wireOp",EDGE,"E33"),sQuery(id+"F0.wireOp",EDGE,"E37"),sQuery(id+"F0.wireOp",EDGE,"E38")])],"isStart":false}),makeQuery(id+"F6.opExtrude","CAP_FACE",FACE,{"disambiguationData":[OSD([subQ7,subQ6,subQ5,subQ4])],"isStart":false}),makeQuery(id+"F6.opExtrude","CAP_FACE",FACE,{"disambiguationData":[OSD([subQ3,subQ2,subQ1,subQ0])],"isStart":false})]});}
            var sketch = newSketch(context, id + "F7", { "sketchPlane" : qUnion([Q0])});
            skCircle(sketch, "E73", {"center": v(140.86, 10.72) * mm, "radius": 2 * mm});
            skCircle(sketch, "E74", {"center": v(107.2, 92.04) * mm, "radius": 2 * mm});
            skSolve(sketch);
        }
        {
            var Q0;
            Q0=qSketchRegion(id+"F7",true);
            extrude(context, id + "F8", {"entities" : qUnion([Q0]), "operationType" : NewBodyOperationType.REMOVE, "oppositeDirection" : true, "depth" : 25 * mm});
        }
        {
            var Q0;
            Q0=makeQuery(id+"F0.imprint","IMPRINT",FACE,{"disambiguationData":[TD([[makeQuery(id+"F0.imprint","IMPRINT",EDGE,{"derivedFrom":sQuery(id+"F0.wireOp",EDGE,"E32")}),1.0]])]});
            var Q1;
            Q1=makeQuery(id+"F0.imprint","IMPRINT",FACE,{"disambiguationData":[TD([[makeQuery(id+"F0.imprint","IMPRINT",EDGE,{"derivedFrom":sQuery(id+"F0.wireOp",EDGE,"E33")}),1.0]])]});
            var Q2;
            Q2=makeQuery(id+"F0.imprint","IMPRINT",FACE,{"disambiguationData":[TD([[makeQuery(id+"F0.imprint","IMPRINT",EDGE,{"derivedFrom":sQuery(id+"F0.wireOp",EDGE,"E28")}),1.0]])]});
            var Q3;
            Q3=makeQuery(id+"F0.imprint","IMPRINT",FACE,{"disambiguationData":[TD([[makeQuery(id+"F0.imprint","IMPRINT",EDGE,{"derivedFrom":sQuery(id+"F0.wireOp",EDGE,"E27")}),1.0]])]});
            extrude(context, id + "F9", {"entities" : qUnion([Q0, Q1, Q2, Q3]), "operationType" : NewBodyOperationType.ADD, "depth" : 2.5 * mm});
        }
        {
            var Q0;
            {var subQ0=sQuery(id+"F2.wireOp",EDGE,"E71");var subQ1=makeQuery(id+"F1.opExtrude","CAP_EDGE",EDGE,{"disambiguationData":[OSD([sQuery(id+"F0.wireOp",EDGE,"E22")])],"isStart":false});var subQ2=makeQuery(id+"F2.imprint","INTERSECT",VERTEX,{"derivedFrom":[subQ1,subQ0]});Q0=makeQuery(id+"F2.imprint","IMPRINT",FACE,{"disambiguationData":[TD([[makeQuery(id+"F2.imprint","IMPRINT",EDGE,{"disambiguationData":[TD([[subQ2,-1.0]])],"derivedFrom":subQ0}),1.0]])]});}
            var Q1;
            Q1=makeQuery(id+"F2.imprint","IMPRINT",FACE,{"disambiguationData":[TD([[makeQuery(id+"F2.imprint","IMPRINT",EDGE,{"derivedFrom":makeQuery(id+"F1.opExtrude","CAP_EDGE",EDGE,{"disambiguationData":[OSD([sQuery(id+"F0.wireOp",EDGE,"E28")])],"isStart":false})}),-1.0]])]});
            var Q2;
            Q2=makeQuery(id+"F2.imprint","IMPRINT",FACE,{"disambiguationData":[TD([[makeQuery(id+"F2.imprint","IMPRINT",EDGE,{"derivedFrom":makeQuery(id+"F1.opExtrude","CAP_EDGE",EDGE,{"disambiguationData":[OSD([sQuery(id+"F0.wireOp",EDGE,"E28")])],"isStart":false})}),1.0]])]});
            var Q3;
            {var subQ0=sQuery(id+"F2.wireOp",EDGE,"E62");var subQ3=sQuery(id+"F2.wireOp",EDGE,"E71");var subQ4=makeQuery(id+"F2.imprint","INTERSECT",VERTEX,{"derivedFrom":[subQ0,subQ3]});Q3=makeQuery(id+"F2.imprint","IMPRINT",FACE,{"disambiguationData":[TD([[makeQuery(id+"F2.imprint","IMPRINT",EDGE,{"disambiguationData":[TD([[subQ4,1.0]])],"derivedFrom":subQ3}),1.0]])]});}
            var Q4;
            {var subQ0=sQuery(id+"F2.wireOp",EDGE,"E57");Q4=makeQuery(id+"F2.imprint","IMPRINT",FACE,{"disambiguationData":[TD([[makeQuery(id+"F2.imprint","IMPRINT",EDGE,{"derivedFrom":subQ0}),1.0]])]});}
            var Q5;
            {var subQ5=sQuery(id+"F2.wireOp",EDGE,"E57");Q5=makeQuery(id+"F2.imprint","IMPRINT",FACE,{"disambiguationData":[TD([[makeQuery(id+"F2.imprint","IMPRINT",EDGE,{"derivedFrom":subQ5}),-1.0]])]});}
            var Q6;
            Q6=makeQuery(id+"F2.imprint","IMPRINT",FACE,{"disambiguationData":[TD([[makeQuery(id+"F2.imprint","IMPRINT",EDGE,{"derivedFrom":makeQuery(id+"F1.opExtrude","CAP_EDGE",EDGE,{"disambiguationData":[OSD([sQuery(id+"F0.wireOp",EDGE,"E33")])],"isStart":false})}),1.0]])]});
            extrude(context, id + "F10", {"entities" : qUnion([Q0, Q1, Q2, Q3, Q4, Q5, Q6]), "operationType" : NewBodyOperationType.REMOVE, "oppositeDirection" : true, "depth" : 25 * mm});
        }
        {
            var Q0;
            Q0=makeQuery(id+"F10.boolean.opBoolean","COPY",EDGE,{"derivedFrom":makeQuery(id+"F10.opExtrude","CAP_EDGE",EDGE,{"disambiguationData":[OSD([sQuery(id+"F2.wireOp",EDGE,"E72")])],"isStart":true})});
            var Q1;
            Q1=makeQuery(id+"F10.boolean.opBoolean","COPY",EDGE,{"derivedFrom":makeQuery(id+"F10.opExtrude","CAP_EDGE",EDGE,{"disambiguationData":[OSD([sQuery(id+"F2.wireOp",EDGE,"E71")])],"isStart":true})});
            var Q2;
            {var subQ0=sQuery(id+"F0.wireOp",EDGE,"E33");var subQ1=sQuery(id+"F0.wireOp",EDGE,"E32");var subQ2=sQuery(id+"F0.wireOp",EDGE,"E28");var subQ3=sQuery(id+"F0.wireOp",EDGE,"E27");var subQ4=sQuery(id+"F0.wireOp",EDGE,"E24");var subQ5=sQuery(id+"F0.wireOp",EDGE,"E23");var subQ6=sQuery(id+"F0.wireOp",EDGE,"E20");var subQ7=sQuery(id+"F0.wireOp",EDGE,"E19");var subQ8=sQuery(id+"F0.wireOp",EDGE,"E22");var subQ9=sQuery(id+"F0.wireOp",EDGE,"E21");var subQ10=sQuery(id+"F0.wireOp",EDGE,"E13");var subQ11=sQuery(id+"F0.wireOp",EDGE,"E12");Q2=makeQuery(id+"F10.boolean.opBoolean","INTERSECT",EDGE,{"derivedFrom":[makeQuery(id+"F9.boolean.opBoolean","MERGE",FACE,{"derivedFrom":[makeQuery(id+"F6.boolean.opBoolean","MERGE",FACE,{"derivedFrom":[makeQuery(id+"F1.opExtrude","CAP_FACE",FACE,{"disambiguationData":[OSD([sQuery(id+"F0.wireOp",EDGE,"E0"),sQuery(id+"F0.wireOp",EDGE,"E1"),sQuery(id+"F0.wireOp",EDGE,"E8"),sQuery(id+"F0.wireOp",EDGE,"E9"),sQuery(id+"F0.wireOp",EDGE,"E10"),sQuery(id+"F0.wireOp",EDGE,"E11"),subQ11,subQ10,sQuery(id+"F0.wireOp",EDGE,"E15"),sQuery(id+"F0.wireOp",EDGE,"E16"),subQ7,subQ6,subQ9,subQ8,subQ5,subQ4,subQ3,subQ2,subQ1,subQ0,sQuery(id+"F0.wireOp",EDGE,"E37"),sQuery(id+"F0.wireOp",EDGE,"E38")])],"isStart":true}),makeQuery(id+"F6.opExtrude","CAP_FACE",FACE,{"disambiguationData":[OSD([subQ11,subQ10,subQ9,subQ8])],"isStart":true}),makeQuery(id+"F6.opExtrude","CAP_FACE",FACE,{"disambiguationData":[OSD([subQ7,subQ6,subQ5,subQ4])],"isStart":true})]}),makeQuery(id+"F9.opExtrude","CAP_FACE",FACE,{"disambiguationData":[OSD([subQ3])],"isStart":true}),makeQuery(id+"F9.opExtrude","CAP_FACE",FACE,{"disambiguationData":[OSD([subQ2])],"isStart":true}),makeQuery(id+"F9.opExtrude","CAP_FACE",FACE,{"disambiguationData":[OSD([subQ1])],"isStart":true}),makeQuery(id+"F9.opExtrude","CAP_FACE",FACE,{"disambiguationData":[OSD([subQ0])],"isStart":true})]}),makeQuery(id+"F10.opExtrude","SWEPT_FACE",FACE,{"disambiguationData":[OSD([sQuery(id+"F2.wireOp",EDGE,"E71")])]})]});}
            var Q3;
            {var subQ0=sQuery(id+"F0.wireOp",EDGE,"E33");var subQ1=sQuery(id+"F0.wireOp",EDGE,"E32");var subQ2=sQuery(id+"F0.wireOp",EDGE,"E28");var subQ3=sQuery(id+"F0.wireOp",EDGE,"E27");var subQ4=sQuery(id+"F0.wireOp",EDGE,"E24");var subQ5=sQuery(id+"F0.wireOp",EDGE,"E23");var subQ6=sQuery(id+"F0.wireOp",EDGE,"E20");var subQ7=sQuery(id+"F0.wireOp",EDGE,"E19");var subQ8=sQuery(id+"F0.wireOp",EDGE,"E22");var subQ9=sQuery(id+"F0.wireOp",EDGE,"E21");var subQ10=sQuery(id+"F0.wireOp",EDGE,"E13");var subQ11=sQuery(id+"F0.wireOp",EDGE,"E12");Q3=makeQuery(id+"F10.boolean.opBoolean","INTERSECT",EDGE,{"derivedFrom":[makeQuery(id+"F9.boolean.opBoolean","MERGE",FACE,{"derivedFrom":[makeQuery(id+"F6.boolean.opBoolean","MERGE",FACE,{"derivedFrom":[makeQuery(id+"F1.opExtrude","CAP_FACE",FACE,{"disambiguationData":[OSD([sQuery(id+"F0.wireOp",EDGE,"E0"),sQuery(id+"F0.wireOp",EDGE,"E1"),sQuery(id+"F0.wireOp",EDGE,"E8"),sQuery(id+"F0.wireOp",EDGE,"E9"),sQuery(id+"F0.wireOp",EDGE,"E10"),sQuery(id+"F0.wireOp",EDGE,"E11"),subQ11,subQ10,sQuery(id+"F0.wireOp",EDGE,"E15"),sQuery(id+"F0.wireOp",EDGE,"E16"),subQ7,subQ6,subQ9,subQ8,subQ5,subQ4,subQ3,subQ2,subQ1,subQ0,sQuery(id+"F0.wireOp",EDGE,"E37"),sQuery(id+"F0.wireOp",EDGE,"E38")])],"isStart":true}),makeQuery(id+"F6.opExtrude","CAP_FACE",FACE,{"disambiguationData":[OSD([subQ11,subQ10,subQ9,subQ8])],"isStart":true}),makeQuery(id+"F6.opExtrude","CAP_FACE",FACE,{"disambiguationData":[OSD([subQ7,subQ6,subQ5,subQ4])],"isStart":true})]}),makeQuery(id+"F9.opExtrude","CAP_FACE",FACE,{"disambiguationData":[OSD([subQ3])],"isStart":true}),makeQuery(id+"F9.opExtrude","CAP_FACE",FACE,{"disambiguationData":[OSD([subQ2])],"isStart":true}),makeQuery(id+"F9.opExtrude","CAP_FACE",FACE,{"disambiguationData":[OSD([subQ1])],"isStart":true}),makeQuery(id+"F9.opExtrude","CAP_FACE",FACE,{"disambiguationData":[OSD([subQ0])],"isStart":true})]}),makeQuery(id+"F10.opExtrude","SWEPT_FACE",FACE,{"disambiguationData":[OSD([sQuery(id+"F2.wireOp",EDGE,"E72")])]})]});}
            fillet(context, id + "F11", {"entities" : qUnion([Q0, Q1, Q2, Q3]), "radius" : 1 * mm, "tangentPropagation" : true, "allowEdgeOverflow" : false});
        }
        {
            var Q0;
            {var subQ0=sQuery(id+"F0.wireOp",EDGE,"E33");var subQ1=sQuery(id+"F0.wireOp",EDGE,"E32");var subQ2=sQuery(id+"F0.wireOp",EDGE,"E28");var subQ3=sQuery(id+"F0.wireOp",EDGE,"E27");var subQ4=sQuery(id+"F0.wireOp",EDGE,"E24");var subQ5=sQuery(id+"F0.wireOp",EDGE,"E23");var subQ6=sQuery(id+"F0.wireOp",EDGE,"E20");var subQ7=sQuery(id+"F0.wireOp",EDGE,"E19");var subQ8=sQuery(id+"F0.wireOp",EDGE,"E22");var subQ9=sQuery(id+"F0.wireOp",EDGE,"E21");var subQ10=sQuery(id+"F0.wireOp",EDGE,"E13");var subQ11=sQuery(id+"F0.wireOp",EDGE,"E12");Q0=makeQuery(id+"F9.boolean.opBoolean","MERGE",FACE,{"derivedFrom":[makeQuery(id+"F6.boolean.opBoolean","MERGE",FACE,{"derivedFrom":[makeQuery(id+"F1.opExtrude","CAP_FACE",FACE,{"disambiguationData":[OSD([sQuery(id+"F0.wireOp",EDGE,"E0"),sQuery(id+"F0.wireOp",EDGE,"E1"),sQuery(id+"F0.wireOp",EDGE,"E8"),sQuery(id+"F0.wireOp",EDGE,"E9"),sQuery(id+"F0.wireOp",EDGE,"E10"),sQuery(id+"F0.wireOp",EDGE,"E11"),subQ11,subQ10,sQuery(id+"F0.wireOp",EDGE,"E15"),sQuery(id+"F0.wireOp",EDGE,"E16"),subQ7,subQ6,subQ9,subQ8,subQ5,subQ4,subQ3,subQ2,subQ1,subQ0,sQuery(id+"F0.wireOp",EDGE,"E37"),sQuery(id+"F0.wireOp",EDGE,"E38")])],"isStart":false}),makeQuery(id+"F6.opExtrude","CAP_FACE",FACE,{"disambiguationData":[OSD([subQ11,subQ10,subQ9,subQ8])],"isStart":false}),makeQuery(id+"F6.opExtrude","CAP_FACE",FACE,{"disambiguationData":[OSD([subQ7,subQ6,subQ5,subQ4])],"isStart":false})]}),makeQuery(id+"F9.opExtrude","CAP_FACE",FACE,{"disambiguationData":[OSD([subQ3])],"isStart":false}),makeQuery(id+"F9.opExtrude","CAP_FACE",FACE,{"disambiguationData":[OSD([subQ2])],"isStart":false}),makeQuery(id+"F9.opExtrude","CAP_FACE",FACE,{"disambiguationData":[OSD([subQ1])],"isStart":false}),makeQuery(id+"F9.opExtrude","CAP_FACE",FACE,{"disambiguationData":[OSD([subQ0])],"isStart":false})]});}
            var sketch = newSketch(context, id + "F12", { "sketchPlane" : qUnion([Q0])});
            skCircle(sketch, "E75", {"center": v(128.1, 78.07) * mm, "radius": 1.5 * mm});
            skCircle(sketch, "E76", {"center": v(114.87, 69.32) * mm, "radius": 1.5 * mm});
            skCircle(sketch, "E77", {"center": v(130.21, 32.35) * mm, "radius": 1.5 * mm});
            skCircle(sketch, "E78", {"center": v(145.71, 35.4) * mm, "radius": 1.5 * mm});
            skSolve(sketch);
        }
        {
            var Q0;
            Q0=qSketchRegion(id+"F12",true);
            extrude(context, id + "F13", {"entities" : qUnion([Q0]), "operationType" : NewBodyOperationType.REMOVE, "oppositeDirection" : true, "depth" : 25 * mm});
        }
        {
            var Q0;
            {var subQ1=makeQuery(id+"F1.opExtrude","CAP_EDGE",EDGE,{"disambiguationData":[OSD([sQuery(id+"F0.wireOp",EDGE,"E20")])],"isStart":false});Q0=makeQuery(id+"F2.imprint","IMPRINT",FACE,{"disambiguationData":[TD([[makeQuery(id+"F2.imprint","IMPRINT",EDGE,{"derivedFrom":subQ1}),1.0]])]});}
            var sketch = newSketch(context, id + "F14", { "sketchPlane" : qUnion([Q0])});
            skCircle(sketch, "E79", {"center": v(107.2, 92.04) * mm, "radius": 2 * mm});
            skCircle(sketch, "E80", {"center": v(107.2, 92.04) * mm, "radius": 1.5 * mm});
            skSolve(sketch);
        }
        {
            var Q0;
            Q0=qSketchRegion(id+"F14",true);
            extrude(context, id + "F15", {"entities" : qUnion([Q0]), "operationType" : NewBodyOperationType.ADD, "oppositeDirection" : true, "depth" : 2.5 * mm});
        }
        {
            var Q0;
            {var subQ4=makeQuery(id+"F1.opExtrude","CAP_EDGE",EDGE,{"disambiguationData":[OSD([sQuery(id+"F0.wireOp",EDGE,"E13")])],"isStart":false});Q0=makeQuery(id+"F2.imprint","IMPRINT",FACE,{"disambiguationData":[TD([[makeQuery(id+"F2.imprint","IMPRINT",EDGE,{"derivedFrom":subQ4}),-1.0]])]});}
            var sketch = newSketch(context, id + "F16", { "sketchPlane" : qUnion([Q0])});
            skCircle(sketch, "E81", {"center": v(140.86, 10.72) * mm, "radius": 8.25 * mm});
            skCircle(sketch, "E82", {"center": v(107.2, 92.04) * mm, "radius": 8.25 * mm});
            skCircle(sketch, "E83", {"center": v(107.2, 92.04) * mm, "radius": 9.75 * mm});
            skCircle(sketch, "E84", {"center": v(140.86, 10.72) * mm, "radius": 9.75 * mm});
            skSolve(sketch);
        }
        {
            var Q0;
            Q0=makeQuery(id+"F16.imprint","IMPRINT",FACE,{"disambiguationData":[TD([[makeQuery(id+"F16.imprint","IMPRINT",EDGE,{"derivedFrom":sQuery(id+"F16.wireOp",EDGE,"E82")}),1.0]])]});
            var Q1;
            {var subQ0=sQuery(id+"F16.wireOp",EDGE,"E81");var subQ8=makeQuery(id+"F2.imprint","IMPRINT",EDGE,{"derivedFrom":makeQuery(id+"F1.opExtrude","CAP_EDGE",EDGE,{"disambiguationData":[OSD([sQuery(id+"F0.wireOp",EDGE,"E13")])],"isStart":false})});var subQ10=makeQuery(id+"F16.imprint","INTERSECT",VERTEX,{"disambiguationData":[OD(1.0)],"derivedFrom":[subQ8,subQ0]});Q1=makeQuery(id+"F16.imprint","IMPRINT",FACE,{"disambiguationData":[TD([[makeQuery(id+"F16.imprint","IMPRINT",EDGE,{"disambiguationData":[TD([[subQ10,-1.0]])],"derivedFrom":subQ0}),1.0]])]});}
            var Q2;
            {var subQ0=sQuery(id+"F16.wireOp",EDGE,"E81");var subQ1=makeQuery(id+"F2.imprint","IMPRINT",EDGE,{"derivedFrom":makeQuery(id+"F1.opExtrude","CAP_EDGE",EDGE,{"disambiguationData":[OSD([sQuery(id+"F0.wireOp",EDGE,"E21")])],"isStart":false})});var subQ2=makeQuery(id+"F16.imprint","INTERSECT",VERTEX,{"disambiguationData":[OD(0.0)],"derivedFrom":[subQ1,subQ0]});Q2=makeQuery(id+"F16.imprint","IMPRINT",FACE,{"disambiguationData":[TD([[makeQuery(id+"F16.imprint","IMPRINT",EDGE,{"disambiguationData":[TD([[subQ2,-1.0]])],"derivedFrom":subQ0}),1.0]])]});}
            var Q3;
            {var subQ0=sQuery(id+"F16.wireOp",EDGE,"E81");var subQ1=makeQuery(id+"F1.opExtrude","CAP_EDGE",EDGE,{"disambiguationData":[OSD([sQuery(id+"F0.wireOp",EDGE,"E12")])],"isStart":false});var subQ2=makeQuery(id+"F2.imprint","IMPRINT",EDGE,{"disambiguationData":[TD([[makeQuery(id+"F2.imprint","INTERSECT",VERTEX,{"derivedFrom":[subQ1,makeQuery(id+"F1.opExtrude","CAP_EDGE",EDGE,{"disambiguationData":[OSD([sQuery(id+"F0.wireOp",EDGE,"E21")])],"isStart":false})]}),-1.0]])],"derivedFrom":subQ1});var subQ3=makeQuery(id+"F16.imprint","INTERSECT",VERTEX,{"disambiguationData":[OD(0.0)],"derivedFrom":[subQ2,subQ0]});Q3=makeQuery(id+"F16.imprint","IMPRINT",FACE,{"disambiguationData":[TD([[makeQuery(id+"F16.imprint","IMPRINT",EDGE,{"disambiguationData":[TD([[subQ3,1.0]])],"derivedFrom":subQ0}),1.0]])]});}
            var Q4;
            {var subQ0=sQuery(id+"F16.wireOp",EDGE,"E81");var subQ1=makeQuery(id+"F2.imprint","IMPRINT",EDGE,{"derivedFrom":makeQuery(id+"F1.opExtrude","CAP_EDGE",EDGE,{"disambiguationData":[OSD([sQuery(id+"F0.wireOp",EDGE,"E13")])],"isStart":false})});var subQ2=makeQuery(id+"F16.imprint","INTERSECT",VERTEX,{"disambiguationData":[OD(0.0)],"derivedFrom":[subQ1,subQ0]});Q4=makeQuery(id+"F16.imprint","IMPRINT",FACE,{"disambiguationData":[TD([[makeQuery(id+"F16.imprint","IMPRINT",EDGE,{"disambiguationData":[TD([[subQ2,-1.0]])],"derivedFrom":subQ0}),1.0]])]});}
            extrude(context, id + "F17", {"entities" : qUnion([Q0, Q1, Q2, Q3, Q4]), "operationType" : NewBodyOperationType.REMOVE, "oppositeDirection" : true, "depth" : 25 * mm});
        }
        {
            var Q0;
            Q0 = qSketchRegion(id + "F16", true);
            extrude(context, id + "F18", {"entities" : qUnion([Q0]), "operationType" : NewBodyOperationType.ADD, "depth" : 1 * mm});
        }
        {
            var Q0;
            Q0 = qSketchRegion(id + "F16", true);
            extrude(context, id + "F19", {"entities" : qUnion([Q0]), "operationType" : NewBodyOperationType.ADD, "oppositeDirection" : true, "depth" : 2.5 * mm});
        }
    });
